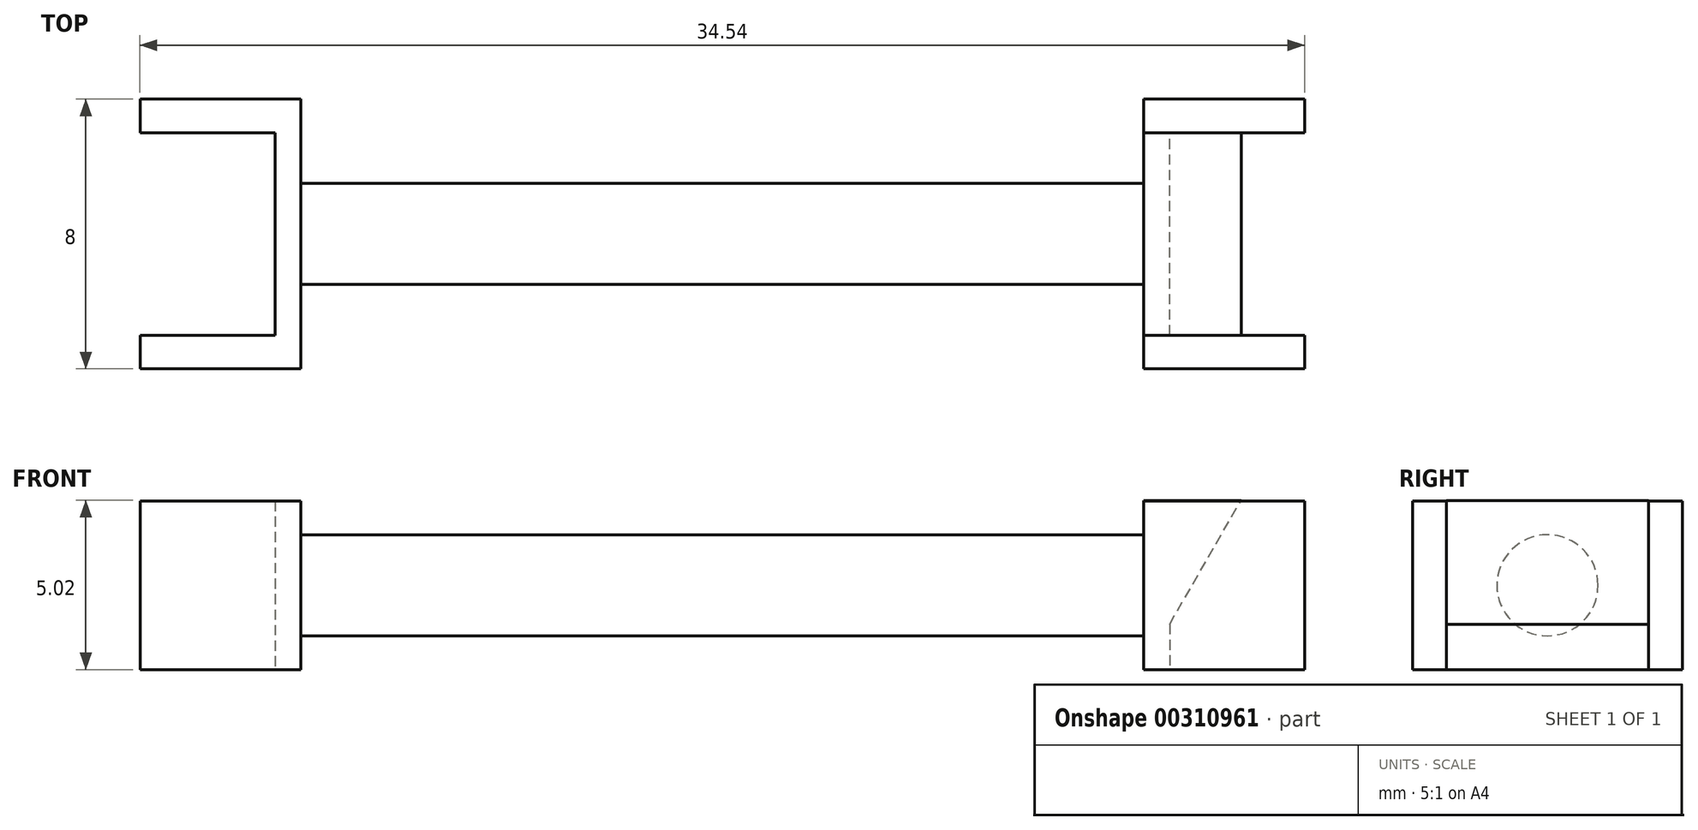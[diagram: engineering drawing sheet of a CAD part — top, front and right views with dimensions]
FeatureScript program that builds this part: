
annotation { "Feature Type Name" : "Feature", "Feature Type Description" : "" }
export const myFeature = defineFeature(function(context is Context, id is Id, definition is map)
    precondition{}
    {
        {
            var Q0;
            Q0=qCreatedBy(makeId("Right.planeOp"),FACE);
            var sketch = newSketch(context, id + "F0", { "sketchPlane" : qUnion([Q0])});
            skCircle(sketch, "E0", {"center": v(0, 0) * mm, "radius": 1.5 * mm});
            skSolve(sketch);
        }
        {
            var Q0;
            Q0 = qSketchRegion(id + "F0", true);
            extrude(context, id + "F1", {"entities" : qUnion([Q0]), "oppositeDirection" : true, "depth" : 12.5 * mm});
        }
        {
            var Q0;
            Q0=qCreatedBy(makeId("Top.planeOp"),FACE);
            var sketch = newSketch(context, id + "F2", { "sketchPlane" : qUnion([Q0])});
            skLineSegment(sketch, "E1.bottom", {"start": v(-12.5, 4) * mm, "end": v(-17.27, 4) * mm});
            skLineSegment(sketch, "E1.top", {"start": v(-12.5, -4) * mm, "end": v(-17.27, -4) * mm});
            skLineSegment(sketch, "E1.left", {"start": v(-12.5, 4) * mm, "end": v(-12.5, -4) * mm});
            skLineSegment(sketch, "E1.right", {"start": v(-17.27, 4) * mm, "end": v(-17.27, 3) * mm});
            skLineSegment(sketch, "E2", {"start": v(0, 0) * mm, "end": v(-12.5, 0) * mm, "construction": true});
            skLineSegment(sketch, "E3.bottom", {"start": v(-17.27, 3) * mm, "end": v(-13.27, 3) * mm});
            skLineSegment(sketch, "E3.top", {"start": v(-17.27, -3) * mm, "end": v(-13.27, -3) * mm});
            skLineSegment(sketch, "E3.right", {"start": v(-13.27, 3) * mm, "end": v(-13.27, -3) * mm});
            skPoint(sketch, "E4", {"position": v(-17.27, 3) * mm});
            skPoint(sketch, "E5", {"position": v(-17.27, -3) * mm});
            skLineSegment(sketch, "E6.trimOffspring", {"start": v(-17.27, -3) * mm, "end": v(-17.27, -4) * mm});
            skPoint(sketch, "E7", {"position": v(-13.27, 0) * mm});
            skLineSegment(sketch, "E8", {"start": v(-13.27, 0) * mm, "end": v(-12.5, 0) * mm, "construction": true});
            skLineSegment(sketch, "E9", {"start": v(-17.27, 4) * mm, "end": v(-17.27, -4) * mm, "construction": true});
            skLineSegment(sketch, "E10", {"start": v(-13.27, 0) * mm, "end": v(-17.27, 0) * mm, "construction": true});
            skSolve(sketch);
        }
        {
            var Q0;
            Q0=makeQuery(id+"F2.imprint","IMPRINT",FACE,{"disambiguationData":[TD([[makeQuery(id+"F2.imprint","IMPRINT",EDGE,{"derivedFrom":sQuery(id+"F2.wireOp",EDGE,"E1.bottom")}),1.0]])]});
            extrude(context, id + "F3", {"entities" : qUnion([Q0]), "operationType" : NewBodyOperationType.ADD, "endBound" : BoundingType.SYMMETRIC, "depth" : 5 * mm});
        }
        {
            var Q0;
            Q0=makeQuery(id+"F1.opExtrude","SWEPT_BODY",BODY,{"disambiguationData":[OSD([sQuery(id+"F0.wireOp",EDGE,"E0")])]});
            var Q1;
            Q1=qCreatedBy(makeId("Right.planeOp"),FACE);
            mirror(context, id + "F4", {"operationType" : NewBodyOperationType.ADD, "entities" : qUnion([Q0]), "mirrorPlane" : qUnion([Q1])});
        }
        {
            var Q0;
            Q0=qCreatedBy(makeId("Front.planeOp"),FACE);
            var sketch = newSketch(context, id + "F5", { "sketchPlane" : qUnion([Q0])});
            skLineSegment(sketch, "E11", {"start": v(12.5, 2.52) * mm, "end": v(12.5, -2.48) * mm});
            skLineSegment(sketch, "E12", {"start": v(12.5, -2.48) * mm, "end": v(15.39, 2.52) * mm});
            skLineSegment(sketch, "E13", {"start": v(15.39, 2.52) * mm, "end": v(12.5, 2.52) * mm});
            skLineSegment(sketch, "E14", {"start": v(12.5, 0) * mm, "end": v(0, 0) * mm, "construction": true});
            skSolve(sketch);
        }
        {
            var Q0;
            Q0=makeQuery(id+"F5.imprint","IMPRINT",FACE,{"disambiguationData":[TD([[makeQuery(id+"F5.imprint","IMPRINT",EDGE,{"derivedFrom":sQuery(id+"F5.wireOp",EDGE,"E11")}),1.0]])]});
            extrude(context, id + "F6", {"entities" : qUnion([Q0]), "operationType" : NewBodyOperationType.ADD, "endBound" : BoundingType.SYMMETRIC, "depth" : 6 * mm});
        }
    });
